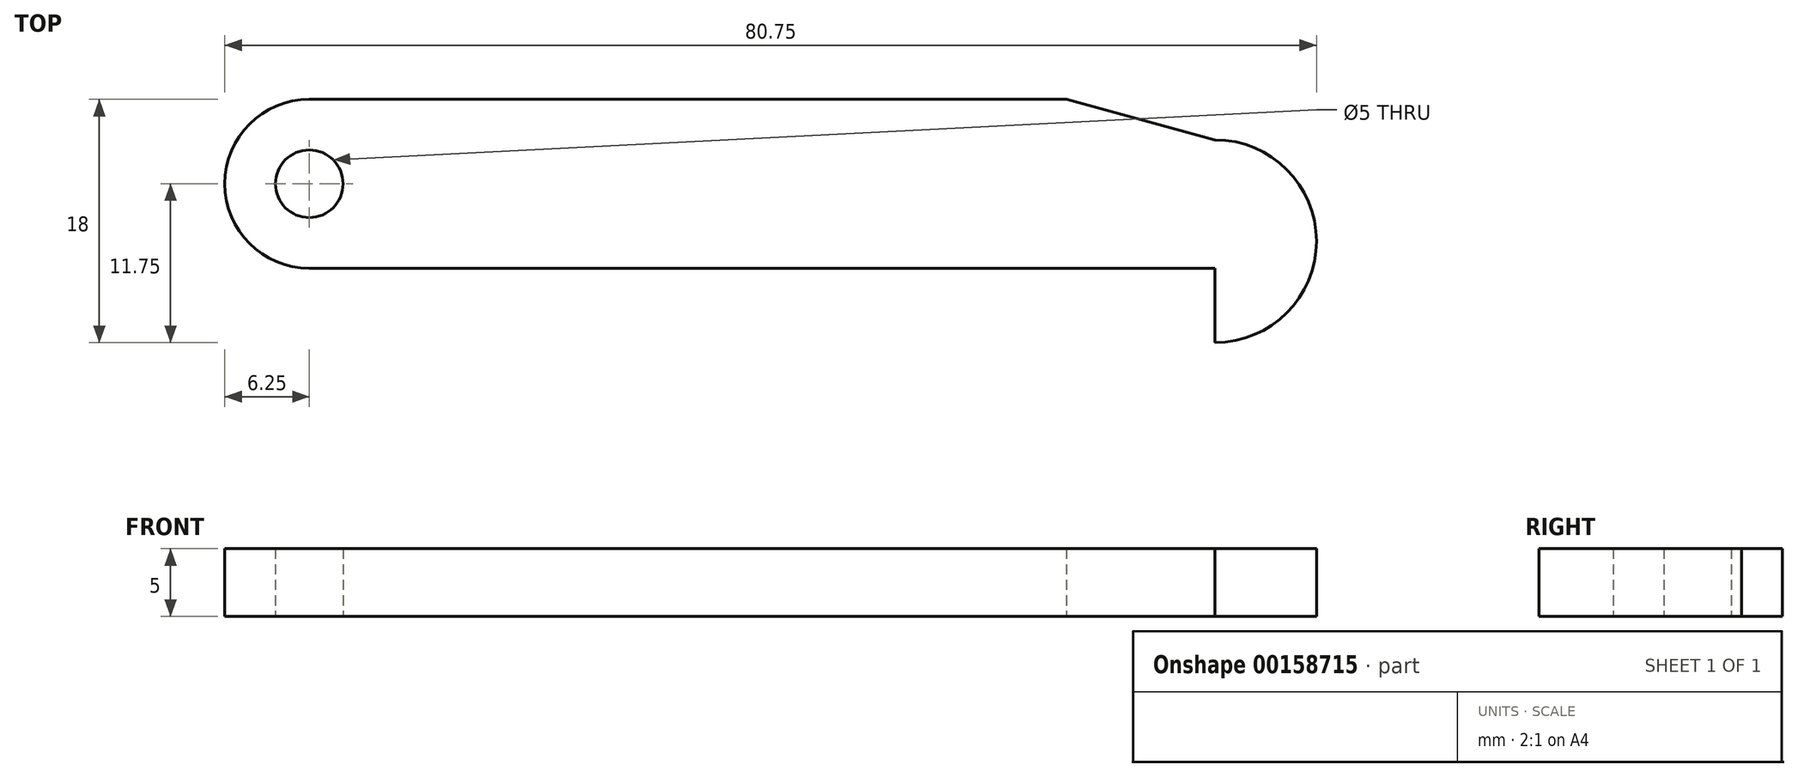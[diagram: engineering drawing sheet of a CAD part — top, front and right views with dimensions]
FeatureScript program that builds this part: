
annotation { "Feature Type Name" : "Feature", "Feature Type Description" : "" }
export const myFeature = defineFeature(function(context is Context, id is Id, definition is map)
    precondition{}
    {
        {
            var Q0;
            Q0=qCreatedBy(makeId("Top.planeOp"),FACE);
            var sketch = newSketch(context, id + "F0", { "sketchPlane" : qUnion([Q0])});
            skLineSegment(sketch, "E0", {"start": v(0, 6.25) * mm, "end": v(-56, 6.25) * mm});
            skLineSegment(sketch, "E1", {"start": v(11, -6.25) * mm, "end": v(11, -11.75) * mm});
            skArc(sketch, "E2", {"start": v(11, -11.75) * mm, "mid": v(18.5, -4.25) * mm, "end": v(11, 3.25) * mm});
            skArc(sketch, "E3", {"start": v(-56, 6.25) * mm, "mid": v(-62.25, 0) * mm, "end": v(-56, -6.25) * mm});
            skCircle(sketch, "E4", {"center": v(-56, 0) * mm, "radius": 2.5 * mm});
            skLineSegment(sketch, "E5", {"start": v(-56, -6.25) * mm, "end": v(11, -6.25) * mm});
            skLineSegment(sketch, "E6", {"start": v(11, 3.25) * mm, "end": v(0, 6.25) * mm});
            skSolve(sketch);
        }
        {
            var Q0;
            Q0 = qSketchRegion(id + "F0", true);
            extrude(context, id + "F1", {"entities" : qUnion([Q0]), "depth" : 5 * mm});
        }
    });
